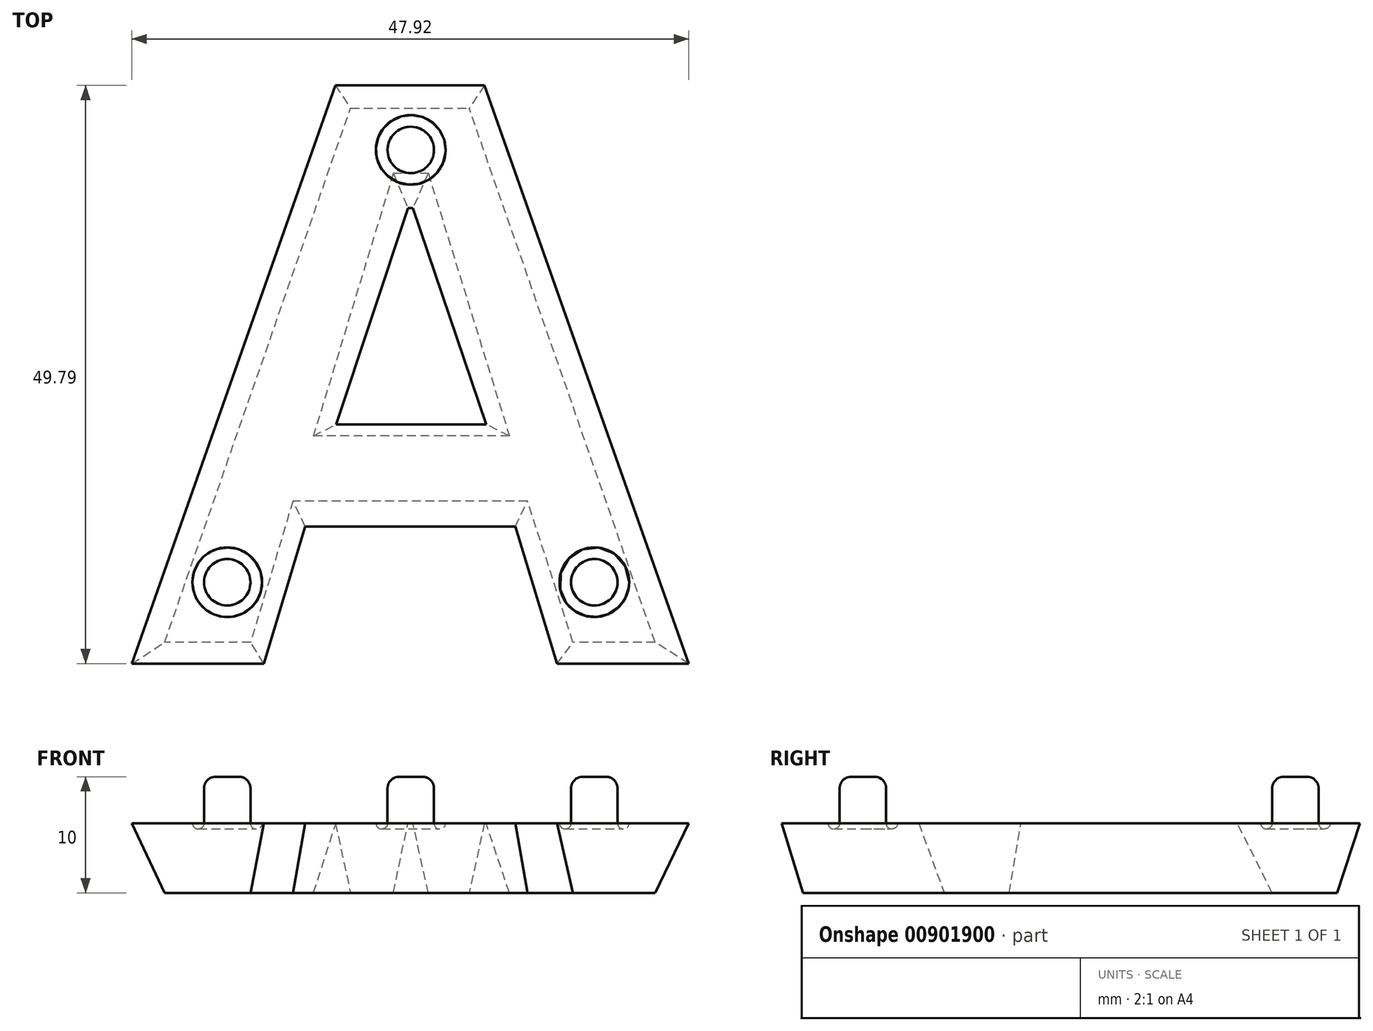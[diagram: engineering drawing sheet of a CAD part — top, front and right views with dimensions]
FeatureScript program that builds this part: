
annotation { "Feature Type Name" : "Feature", "Feature Type Description" : "" }
export const myFeature = defineFeature(function(context is Context, id is Id, definition is map)
    precondition{}
    {
        {
            var Q0;
            Q0=qCreatedBy(makeId("Top.planeOp"),FACE);
            cPlane(context, id + "F0", {"entities" : qUnion([Q0]), "cplaneType" : CPlaneType.OFFSET, "offset" : 6 * mm, "width" : 150 * mm, "height" : 150 * mm});
        }
        {
            var Q0;
            Q0=qCreatedBy(id+"F0.planeOp",FACE);
            var sketch = newSketch(context, id + "F1", { "sketchPlane" : qUnion([Q0])});
            skLineSegment(sketch, "E0", {"start": v(0, 0) * mm, "end": v(17.51, 49.8) * mm});
            skLineSegment(sketch, "E1", {"start": v(17.51, 49.8) * mm, "end": v(30.34, 49.8) * mm});
            skLineSegment(sketch, "E2", {"start": v(30.34, 49.8) * mm, "end": v(47.92, 0) * mm});
            skLineSegment(sketch, "E3", {"start": v(47.92, 0) * mm, "end": v(36.59, 0) * mm});
            skLineSegment(sketch, "E4", {"start": v(36.59, 0) * mm, "end": v(33, 11.8) * mm});
            skLineSegment(sketch, "E5", {"start": v(33, 11.8) * mm, "end": v(14.92, 11.8) * mm});
            skLineSegment(sketch, "E6", {"start": v(14.92, 11.8) * mm, "end": v(11.34, 0) * mm});
            skLineSegment(sketch, "E7", {"start": v(11.34, 0) * mm, "end": v(0, 0) * mm});
            skPoint(sketch, "E8.end.orphan", {"position": v(23.97, 42.08) * mm});
            skSolve(sketch);
        }
        {
            var Q0;
            Q0=qCreatedBy(makeId("Top.planeOp"),FACE);
            var sketch = newSketch(context, id + "F2", { "sketchPlane" : qUnion([Q0])});
            skLineSegment(sketch, "E9", {"start": v(45.03, 1.84) * mm, "end": v(37.97, 1.84) * mm});
            skLineSegment(sketch, "E10", {"start": v(37.97, 1.84) * mm, "end": v(34.05, 14) * mm});
            skLineSegment(sketch, "E11", {"start": v(34.05, 14) * mm, "end": v(13.85, 14) * mm});
            skLineSegment(sketch, "E12", {"start": v(13.85, 14) * mm, "end": v(10.22, 1.84) * mm});
            skLineSegment(sketch, "E13", {"start": v(10.22, 1.84) * mm, "end": v(2.8, 1.84) * mm});
            skLineSegment(sketch, "E14", {"start": v(2.8, 1.84) * mm, "end": v(18.82, 47.84) * mm});
            skLineSegment(sketch, "E15", {"start": v(18.82, 47.84) * mm, "end": v(29.02, 47.84) * mm});
            skLineSegment(sketch, "E16", {"start": v(45.03, 1.84) * mm, "end": v(29.02, 47.84) * mm});
            skLineSegment(sketch, "E17", {"start": v(37.97, 1.84) * mm, "end": v(34.05, 14) * mm, "construction": true});
            skSolve(sketch);
        }
        {
            var Q0;
            Q0=qCreatedBy(id+"F0.planeOp",FACE);
            cPlane(context, id + "F3", {"entities" : qUnion([Q0]), "cplaneType" : CPlaneType.OFFSET, "offset" : 5 * mm, "width" : 150 * mm, "height" : 150 * mm});
        }
        {
            var Q0;
            Q0=qCreatedBy(makeId("Top.planeOp"),FACE);
            cPlane(context, id + "F4", {"entities" : qUnion([Q0]), "cplaneType" : CPlaneType.OFFSET, "offset" : 5 * mm, "oppositeDirection" : true, "width" : 150 * mm, "height" : 150 * mm});
        }
        {
            var Q0;
            Q0=makeQuery(id+"F1.imprint","IMPRINT",FACE,{"disambiguationData":[TD([[makeQuery(id+"F1.imprint","IMPRINT",EDGE,{"derivedFrom":sQuery(id+"F1.wireOp",EDGE,"E0")}),-1.0]])]});
            var Q1;
            Q1=makeQuery(id+"F2.imprint","IMPRINT",FACE,{"disambiguationData":[TD([[makeQuery(id+"F2.imprint","IMPRINT",EDGE,{"derivedFrom":sQuery(id+"F2.wireOp",EDGE,"E9")}),-1.0]])]});
            loft(context, id + "F5", {"sheetProfilesArray" : [{ "sheetProfileEntities" : qUnion([Q0]) }, { "sheetProfileEntities" : qUnion([Q1]) }]});
        }
        {
            var Q0;
            Q0=makeQuery(id+"F1.imprint","IMPRINT",FACE,{"disambiguationData":[TD([[makeQuery(id+"F1.imprint","IMPRINT",EDGE,{"derivedFrom":sQuery(id+"F1.wireOp",EDGE,"E0")}),-1.0]])]});
            var sketch = newSketch(context, id + "F6", { "sketchPlane" : qUnion([Q0])});
            skLineSegment(sketch, "E18", {"start": v(17.57, 20.6) * mm, "end": v(30.48, 20.6) * mm});
            skLineSegment(sketch, "E19", {"start": v(30.48, 20.6) * mm, "end": v(24.2, 39.24) * mm});
            skLineSegment(sketch, "E20", {"start": v(23.75, 39.24) * mm, "end": v(17.57, 20.6) * mm});
            skLineSegment(sketch, "E21", {"start": v(23.75, 39.24) * mm, "end": v(24.2, 39.24) * mm});
            skSolve(sketch);
        }
        {
            var Q0;
            Q0=makeQuery(id+"F2.imprint","IMPRINT",FACE,{"disambiguationData":[TD([[makeQuery(id+"F2.imprint","IMPRINT",EDGE,{"derivedFrom":sQuery(id+"F2.wireOp",EDGE,"E9")}),-1.0]])]});
            var sketch = newSketch(context, id + "F7", { "sketchPlane" : qUnion([Q0])});
            skLineSegment(sketch, "E22", {"start": v(32.48, 19.6) * mm, "end": v(15.62, 19.6) * mm});
            skLineSegment(sketch, "E23", {"start": v(22.5, 42.24) * mm, "end": v(25.5, 42.24) * mm});
            skLineSegment(sketch, "E24", {"start": v(24, 42.24) * mm, "end": v(24, 15.1) * mm, "construction": true});
            skLineSegment(sketch, "E25", {"start": v(25.5, 42.24) * mm, "end": v(37.96, 1.84) * mm, "construction": true});
            skLineSegment(sketch, "E26", {"start": v(22.5, 42.24) * mm, "end": v(8.33, -4.36) * mm, "construction": true});
            skPoint(sketch, "E27.end.orphan", {"position": v(31.77, 19.6) * mm});
            skPoint(sketch, "E28.start.orphan", {"position": v(16.2, 19.6) * mm});
            skLineSegment(sketch, "E29", {"start": v(25.5, 42.24) * mm, "end": v(32.48, 19.6) * mm});
            skLineSegment(sketch, "E30", {"start": v(22.5, 42.24) * mm, "end": v(15.62, 19.6) * mm});
            skSolve(sketch);
        }
        {
            var Q0;
            Q0=makeQuery(id+"F7.imprint","IMPRINT",FACE,{"disambiguationData":[TD([[makeQuery(id+"F7.imprint","IMPRINT",EDGE,{"derivedFrom":sQuery(id+"F7.wireOp",EDGE,"E22")}),-1.0]])]});
            var Q1;
            Q1=makeQuery(id+"F6.imprint","IMPRINT",FACE,{"disambiguationData":[TD([[makeQuery(id+"F6.imprint","IMPRINT",EDGE,{"derivedFrom":sQuery(id+"F6.wireOp",EDGE,"E18")}),1.0]])]});
            loft(context, id + "F8", {"operationType" : NewBodyOperationType.REMOVE, "sheetProfilesArray" : [{ "sheetProfileEntities" : qUnion([Q0]) }, { "sheetProfileEntities" : qUnion([Q1]) }]});
        }
        {
            var Q0;
            Q0=makeQuery(id+"F1.imprint","IMPRINT",FACE,{"disambiguationData":[TD([[makeQuery(id+"F1.imprint","IMPRINT",EDGE,{"derivedFrom":sQuery(id+"F1.wireOp",EDGE,"E0")}),-1.0]])]});
            var sketch = newSketch(context, id + "F9", { "sketchPlane" : qUnion([Q0])});
            skCircle(sketch, "E31", {"center": v(24, 44.24) * mm, "radius": 3 * mm});
            skCircle(sketch, "E32", {"center": v(8.2, 7) * mm, "radius": 3 * mm});
            skCircle(sketch, "E33", {"center": v(39.8, 7) * mm, "radius": 3 * mm});
            skCircle(sketch, "E34", {"center": v(24, 44.24) * mm, "radius": 2 * mm});
            skCircle(sketch, "E35", {"center": v(39.8, 7) * mm, "radius": 2 * mm});
            skCircle(sketch, "E36", {"center": v(8.2, 7) * mm, "radius": 2 * mm});
            skSolve(sketch);
        }
        {
            var Q0;
            Q0=makeQuery(id+"F9.imprint","IMPRINT",FACE,{"disambiguationData":[TD([[makeQuery(id+"F9.imprint","IMPRINT",EDGE,{"derivedFrom":sQuery(id+"F9.wireOp",EDGE,"E36")}),1.0]])]});
            var Q1;
            Q1=makeQuery(id+"F9.imprint","IMPRINT",FACE,{"disambiguationData":[TD([[makeQuery(id+"F9.imprint","IMPRINT",EDGE,{"derivedFrom":sQuery(id+"F9.wireOp",EDGE,"E34")}),1.0]])]});
            var Q2;
            Q2=makeQuery(id+"F9.imprint","IMPRINT",FACE,{"disambiguationData":[TD([[makeQuery(id+"F9.imprint","IMPRINT",EDGE,{"derivedFrom":sQuery(id+"F9.wireOp",EDGE,"E35")}),1.0]])]});
            var Q3;
            Q3=sQuery(id+"F9.wireOp",EDGE,"E36");
            var Q4;
            Q4=sQuery(id+"F9.wireOp",EDGE,"E34");
            var Q5;
            Q5=sQuery(id+"F9.wireOp",EDGE,"E35");
            extrude(context, id + "F10", {"entities" : qUnion([Q0, Q1, Q2]), "operationType" : NewBodyOperationType.ADD, "surfaceEntities" : qUnion([Q3, Q4, Q5]), "depth" : 4 * mm, "offsetDistance" : 25 * mm});
        }
        {
            var Q0;
            Q0=makeQuery(id+"F9.imprint","IMPRINT",FACE,{"disambiguationData":[TD([[makeQuery(id+"F9.imprint","IMPRINT",EDGE,{"derivedFrom":sQuery(id+"F9.wireOp",EDGE,"E32")}),1.0]])]});
            var Q1;
            Q1=sQuery(id+"F9.wireOp",EDGE,"E36");
            var Q2;
            Q2=sQuery(id+"F9.wireOp",EDGE,"E32");
            extrude(context, id + "F11", {"entities" : qUnion([Q0]), "operationType" : NewBodyOperationType.REMOVE, "surfaceEntities" : qUnion([Q1, Q2]), "oppositeDirection" : true, "depth" : 1 * mm, "offsetDistance" : 25 * mm});
        }
        {
            var Q0;
            Q0=makeQuery(id+"F9.imprint","IMPRINT",FACE,{"disambiguationData":[TD([[makeQuery(id+"F9.imprint","IMPRINT",EDGE,{"derivedFrom":sQuery(id+"F9.wireOp",EDGE,"E33")}),1.0]])]});
            var Q1;
            Q1=sQuery(id+"F9.wireOp",EDGE,"E35");
            var Q2;
            Q2=sQuery(id+"F9.wireOp",EDGE,"E33");
            extrude(context, id + "F12", {"entities" : qUnion([Q0]), "operationType" : NewBodyOperationType.REMOVE, "surfaceEntities" : qUnion([Q1, Q2]), "oppositeDirection" : true, "depth" : 1 * mm, "offsetDistance" : 25 * mm});
        }
        {
            var Q0;
            Q0=makeQuery(id+"F9.imprint","IMPRINT",FACE,{"disambiguationData":[TD([[makeQuery(id+"F9.imprint","IMPRINT",EDGE,{"derivedFrom":sQuery(id+"F9.wireOp",EDGE,"E31")}),1.0]])]});
            var Q1;
            Q1=sQuery(id+"F9.wireOp",EDGE,"E34");
            var Q2;
            Q2=sQuery(id+"F9.wireOp",EDGE,"E31");
            extrude(context, id + "F13", {"entities" : qUnion([Q0]), "operationType" : NewBodyOperationType.REMOVE, "surfaceEntities" : qUnion([Q1, Q2]), "oppositeDirection" : true, "depth" : 1 * mm, "offsetDistance" : 25 * mm});
        }
        {
            var Q0;
            Q0=makeQuery(id+"F11.boolean.opBoolean","COPY",EDGE,{"derivedFrom":makeQuery(id+"F11.opExtrude","CAP_EDGE",EDGE,{"disambiguationData":[OSD([sQuery(id+"F9.wireOp",EDGE,"E36")])],"isStart":false})});
            fillet(context, id + "F14", {"entities" : qUnion([Q0]), "tangentPropagation" : true, "radius" : 1 * mm, "defaultsChanged" : false, "vertexSettings" : [], "allowEdgeOverflow" : false});
        }
        {
            var Q0;
            Q0=makeQuery(id+"F14.opFillet","BLEND_EDGE",EDGE,{"blendedFrom":[makeQuery(id+"F11.boolean.opBoolean","COPY",EDGE,{"derivedFrom":makeQuery(id+"F11.opExtrude","CAP_EDGE",EDGE,{"disambiguationData":[OSD([sQuery(id+"F9.wireOp",EDGE,"E36")])],"isStart":false})}),makeQuery(id+"F11.boolean.opBoolean","COPY",FACE,{"derivedFrom":makeQuery(id+"F11.opExtrude","SWEPT_FACE",FACE,{"disambiguationData":[OSD([sQuery(id+"F9.wireOp",EDGE,"E32")])]})})],"blendedInto":[makeQuery(id+"F11.boolean.opBoolean","COPY",FACE,{"derivedFrom":makeQuery(id+"F11.opExtrude","SWEPT_FACE",FACE,{"disambiguationData":[OSD([sQuery(id+"F9.wireOp",EDGE,"E32")])]})})]});
            fillet(context, id + "F15", {"entities" : qUnion([Q0]), "tangentPropagation" : true, "radius" : 0.5 * mm, "defaultsChanged" : true, "vertexSettings" : [], "allowEdgeOverflow" : false});
        }
        {
            var Q0;
            Q0=makeQuery(id+"F10.opExtrude","CAP_EDGE",EDGE,{"disambiguationData":[OSD([sQuery(id+"F9.wireOp",EDGE,"E36")])],"isStart":false});
            fillet(context, id + "F16", {"entities" : qUnion([Q0]), "tangentPropagation" : true, "radius" : 1 * mm, "defaultsChanged" : true, "vertexSettings" : [], "allowEdgeOverflow" : false});
        }
        {
            var Q0;
            Q0=makeQuery(id+"F10.opExtrude","CAP_EDGE",EDGE,{"disambiguationData":[OSD([sQuery(id+"F9.wireOp",EDGE,"E35")])],"isStart":false});
            fillet(context, id + "F17", {"entities" : qUnion([Q0]), "tangentPropagation" : true, "radius" : 1 * mm, "defaultsChanged" : true, "vertexSettings" : [], "allowEdgeOverflow" : false});
        }
        {
            var Q0;
            Q0=makeQuery(id+"F10.opExtrude","CAP_EDGE",EDGE,{"disambiguationData":[OSD([sQuery(id+"F9.wireOp",EDGE,"E34")])],"isStart":false});
            fillet(context, id + "F18", {"entities" : qUnion([Q0]), "tangentPropagation" : true, "radius" : 1 * mm, "defaultsChanged" : true, "vertexSettings" : [], "allowEdgeOverflow" : false});
        }
        {
            var Q0;
            Q0=makeQuery(id+"F13.boolean.opBoolean","COPY",EDGE,{"derivedFrom":makeQuery(id+"F13.opExtrude","CAP_EDGE",EDGE,{"disambiguationData":[OSD([sQuery(id+"F9.wireOp",EDGE,"E34")])],"isStart":false})});
            fillet(context, id + "F19", {"entities" : qUnion([Q0]), "tangentPropagation" : true, "radius" : 1 * mm, "defaultsChanged" : true, "vertexSettings" : [], "allowEdgeOverflow" : false});
        }
        {
            var Q0;
            Q0=makeQuery(id+"F19.opFillet","BLEND_EDGE",EDGE,{"blendedFrom":[makeQuery(id+"F13.boolean.opBoolean","COPY",EDGE,{"derivedFrom":makeQuery(id+"F13.opExtrude","CAP_EDGE",EDGE,{"disambiguationData":[OSD([sQuery(id+"F9.wireOp",EDGE,"E34")])],"isStart":false})}),makeQuery(id+"F13.boolean.opBoolean","COPY",FACE,{"derivedFrom":makeQuery(id+"F13.opExtrude","SWEPT_FACE",FACE,{"disambiguationData":[OSD([sQuery(id+"F9.wireOp",EDGE,"E31")])]})})],"blendedInto":[makeQuery(id+"F13.boolean.opBoolean","COPY",FACE,{"derivedFrom":makeQuery(id+"F13.opExtrude","SWEPT_FACE",FACE,{"disambiguationData":[OSD([sQuery(id+"F9.wireOp",EDGE,"E31")])]})})]});
            fillet(context, id + "F20", {"entities" : qUnion([Q0]), "tangentPropagation" : true, "radius" : 0.5 * mm, "defaultsChanged" : true, "vertexSettings" : [], "allowEdgeOverflow" : false});
        }
        {
            var Q0;
            Q0=makeQuery(id+"F12.boolean.opBoolean","COPY",EDGE,{"derivedFrom":makeQuery(id+"F12.opExtrude","CAP_EDGE",EDGE,{"disambiguationData":[OSD([sQuery(id+"F9.wireOp",EDGE,"E35")])],"isStart":false})});
            fillet(context, id + "F21", {"entities" : qUnion([Q0]), "tangentPropagation" : true, "radius" : 1 * mm, "defaultsChanged" : false, "vertexSettings" : [], "allowEdgeOverflow" : false});
        }
        {
            var Q0;
            Q0=makeQuery(id+"F21.opFillet","BLEND_EDGE",EDGE,{"blendedFrom":[makeQuery(id+"F12.boolean.opBoolean","COPY",EDGE,{"derivedFrom":makeQuery(id+"F12.opExtrude","CAP_EDGE",EDGE,{"disambiguationData":[OSD([sQuery(id+"F9.wireOp",EDGE,"E35")])],"isStart":false})}),makeQuery(id+"F12.boolean.opBoolean","COPY",FACE,{"derivedFrom":makeQuery(id+"F12.opExtrude","SWEPT_FACE",FACE,{"disambiguationData":[OSD([sQuery(id+"F9.wireOp",EDGE,"E33")])]})})],"blendedInto":[makeQuery(id+"F12.boolean.opBoolean","COPY",FACE,{"derivedFrom":makeQuery(id+"F12.opExtrude","SWEPT_FACE",FACE,{"disambiguationData":[OSD([sQuery(id+"F9.wireOp",EDGE,"E33")])]})})]});
            fillet(context, id + "F22", {"entities" : qUnion([Q0]), "tangentPropagation" : true, "radius" : 0.5 * mm, "defaultsChanged" : true, "vertexSettings" : [], "allowEdgeOverflow" : false});
        }
    });
